# Revit family: Water_Heater-Commercial-Condensing-Lochinvar-Shield-SWH_Series
name_source: partatom
category: Mechanical Equipment
revit_build: Autodesk Revit 2016 (Build: 20150714_1515(x64)
units: mm (PartAtom-declared; Revit-internal decimal feet)

## family parameters
Cut with Voids When Loaded = No
Host = Face
OmniClass Number = 23.65.35.11
OmniClass Title = Supply Water Heaters
Part Type = Normal
Room Calculation Point = No
Round Connector Dimension = Use Diameter
Shared = Yes

## types (10) — shared parameters
Amperage 1 Phase - 120V - 60Hz = Yes
Assembly Code = D3020100
Audible Alarm Kit = No
BACnet Communication = No
CON·X·US® Remote Connectivity = No
Cold Water Connection Description = Cold Water Connection Inlet 1 1/2"
Cold Water Connection Diameter = 1 1/2"
Concentric Vent Kit = No
Condensate Drain Connection Diameter = 3/4"
Condensate Neutralization Kit = No
Default Elevation = 0"
Description = SHIELD COMMERCIAL WATER HEATER
Direct Venting = Yes
Drain Connection Diameter = 3/4"
Drain Radius = 3/8"
Finish = Metal-Lochinvar-Steel/Glass-Lined
Fuel Type = N - Natural Gas
Hot Water Connection Description = Hot Water Connection Outlet 1 1/2"
Hot Water Connection Diameter = 2"
Inlet D from Front Central = 3"
L - LP Gas = No
Low Water Cutoff Kit = No
Manufacturer = Lochinvar
Material = Metal-Lochinvar-Steel/Glass-Lined
Modbus Communication = No
N - Natural Gas = Yes
Operating Temperature = up to 180˚F
Outlet D From Right Edge = 2 21/32"
Power Supply Description = 120V/1PH/60Hz Power Supply
Price = Prices may vary. Please consult Manufacturer Representative for most up-to-date price list.
Product Documentation Link = https://www.lochinvar.com
Product Page URL = https://www.lochinvar.com
Sidewall Vent Termination Kit = No
T & P Connection Description = 3/4" Relief Connection
T & P Valve Opening Diameter = 3/4"
Turn-Down = 5:1
URL = http://www.lochinvar.com
Vent Cover Plate = No
Voltage = 120 V
Warranty Documentation Link = https://www.lochinvar.com
Water conn Radius = 3/4"
Working Pressure = 150.00 psi

## per-type parameters (varying)
- SWR125*: A=62 1/2"; ASME Tank Construction=No; Air Inlet D From Front Center=1 1/2"; Air Inlet D from Right Edge=6 27/32"; Air Inlet Radius=1 1/2"; Air Intake Connection Description=Air Intake Connection 3''; Air Intake Connection Diameter=3"; B=28"; BTU/hr Input=125000.0 Btu/h; Control Panel Radius1=14 1/2"; Control Panel Radius2=15"; D=29 1/2"; E=46 1/2"; Exhaust Air Connection Description=Exhaust Air Connection 3"; Exhaust Air Connection Diameter=3"; Flue D-from-Center=4"; Flue vent Dia.=3"; Flue vent radius=1 1/2"; GPH @ 100° Rise=145; Gallons Storage=65; Gas Connection Description=Gas Supply Connection 1/2"; Gas Off from side Center=5"; Gas Supply Connection Diameter=1/2"; Gas conn Radius=1/4"; Gas off From Front Center=11 1/4"; Height=66"; Inlet D From Right edge=4 1/2"; LP Connection Description=LP Supply Connection 1/2"; Outlet D From Front Central=2 7/8"; Power D From Center=4 15/32"; Power D From Front=1 3/4"; Shipping Weight=377 LBS.; T&P Off from Center=1 7/8"; Tank Radius=14"; Thermal Efficiency=96%
- SWR150*: A=76"; ASME Tank Construction=No; Air Inlet D From Front Center=1 1/2"; Air Inlet D from Right Edge=4 3/32"; Air Inlet Radius=1 1/2"; Air Intake Connection Description=Air Intake Connection 3''; Air Intake Connection Diameter=3"; B=28"; BTU/hr Input=150000.0 Btu/h; Control Panel Radius1=14 1/2"; Control Panel Radius2=15"; D=44"; E=61"; Exhaust Air Connection Description=Exhaust Air Connection 3"; Exhaust Air Connection Diameter=3"; Flue D-from-Center=4"; Flue vent Dia.=3"; Flue vent radius=1 1/2"; GPH @ 100° Rise=175; Gallons Storage=90; Gas Connection Description=Gas Supply Connection 1/2"; Gas Off from side Center=5"; Gas Supply Connection Diameter=1/2"; Gas conn Radius=1/4"; Gas off From Front Center=11 1/4"; Height=79 1/2"; Inlet D From Right edge=4 1/2"; LP Connection Description=LP Supply Connection 1/2"; Outlet D From Front Central=4 7/8"; Power D From Center=4 15/32"; Power D From Front=1 3/4"; Shipping Weight=700 LBS.; T&P Off from Center=1 7/8"; Tank Radius=14"; Thermal Efficiency=96%
- SWR200*: A=76"; ASME Tank Construction=No; Air Inlet D From Front Center=6"; Air Inlet D from Right Edge=3 19/32"; Air Inlet Radius=1 1/2"; Air Intake Connection Description=Air Intake Connection 3''; Air Intake Connection Diameter=3"; B=28"; BTU/hr Input=199000.0 Btu/h; Control Panel Radius1=14 1/2"; Control Panel Radius2=15"; D=44"; E=61"; Exhaust Air Connection Description=Exhaust Air Connection 3"; Exhaust Air Connection Diameter=3"; Flue D-from-Center=4"; Flue vent Dia.=3"; Flue vent radius=1 1/2"; GPH @ 100° Rise=233; Gallons Storage=90; Gas Connection Description=Gas Supply Connection 1/2"; Gas Off from side Center=5"; Gas Supply Connection Diameter=1/2"; Gas conn Radius=1/4"; Gas off From Front Center=11 1/4"; Height=79 1/2"; Inlet D From Right edge=4 1/2"; LP Connection Description=LP Supply Connection 1/2"; Outlet D From Front Central=3 3/8"; Power D From Center=4 15/32"; Power D From Front=1 3/4"; Shipping Weight=725 LBS.; T&P Off from Center=1 7/8"; Tank Radius=14"; Thermal Efficiency=96%
- SWR285*: A=77 1/2"; ASME Tank Construction=No; Air Inlet D From Front Center=8 3/4"; Air Inlet D from Right Edge=5 19/32"; Air Inlet Radius=2"; Air Intake Connection Description=Air Intake Connection 4''; Air Intake Connection Diameter=4"; B=34"; BTU/hr Input=285000.0 Btu/h; Control Panel Radius1=17 1/2"; Control Panel Radius2=18"; D=30 1/2"; E=51 3/4"; Exhaust Air Connection Description=Exhaust Air Connection 4"; Exhaust Air Connection Diameter=4"; Flue D-from-Center=1/4"; Flue vent Dia.=4"; Flue vent radius=2"; GPH @ 100° Rise=328; Gallons Storage=110; Gas Connection Description=Gas Supply Connection 3/4"; Gas Off from side Center=12 1/2"; Gas Supply Connection Diameter=3/4"; Gas conn Radius=3/8"; Gas off From Front Center=8"; Height=79 3/8"; Inlet D From Right edge=2 1/2"; LP Connection Description=LP Supply Connection 3/4"; Outlet D From Front Central=3 3/8"; Power D From Center=2 7/32"; Power D From Front=1 1/4"; Shipping Weight=800 LBS.; T&P Off from Center=1 7/8"; Tank Radius=17"; Thermal Efficiency=95%
- SWR400*: A=77 1/2"; ASME Tank Construction=No; Air Inlet D From Front Center=5 3/4"; Air Inlet D from Right Edge=5 3/32"; Air Inlet Radius=2"; Air Intake Connection Description=Air Intake Connection 4''; Air Intake Connection Diameter=4"; B=34"; BTU/hr Input=399000.0 Btu/h; Control Panel Radius1=17 1/2"; Control Panel Radius2=18"; D=30 1/2"; E=51 3/4"; Exhaust Air Connection Description=Exhaust Air Connection 4"; Exhaust Air Connection Diameter=4"; Flue D-from-Center=14"; Flue vent Dia.=4"; Flue vent radius=2"; GPH @ 100° Rise=459; Gallons Storage=110; Gas Connection Description=Gas Supply Connection 1"; Gas Off from side Center=9 1/2"; Gas Supply Connection Diameter=1"; Gas conn Radius=1/2"; Gas off From Front Center=11 3/4"; Height=79 3/8"; Inlet D From Right edge=2 1/2"; LP Connection Description=LP Supply Connection 1"; Outlet D From Front Central=3 3/8"; Power D From Center=2 7/32"; Power D From Front=1 1/4"; Shipping Weight=850 LBS.; T&P Off from Center=1 7/8"; Tank Radius=17"; Thermal Efficiency=95%
- SWA150*: A=76"; ASME Tank Construction=Yes; Air Inlet D From Front Center=1 1/2"; Air Inlet D from Right Edge=4 3/32"; Air Inlet Radius=1 1/2"; Air Intake Connection Description=Air Intake Connection 3''; Air Intake Connection Diameter=3"; B=28"; BTU/hr Input=150000.0 Btu/h; Control Panel Radius1=14 1/2"; Control Panel Radius2=15"; D=44"; E=61"; Exhaust Air Connection Description=Exhaust Air Connection 3"; Exhaust Air Connection Diameter=3"; Flue D-from-Center=4"; Flue vent Dia.=3"; Flue vent radius=1 1/2"; GPH @ 100° Rise=175; Gallons Storage=90; Gas Connection Description=Gas Supply Connection 1/2"; Gas Off from side Center=5"; Gas Supply Connection Diameter=1/2"; Gas conn Radius=1/4"; Gas off From Front Center=11 1/4"; Height=79 1/2"; Inlet D From Right edge=4 1/2"; LP Connection Description=LP Supply Connection 1/2"; Outlet D From Front Central=4 7/8"; Power D From Center=4 15/32"; Power D From Front=1 3/4"; Shipping Weight=700 LBS.; T&P Off from Center=1 7/8"; Tank Radius=14"; Thermal Efficiency=96%
- SWA200*: A=76"; ASME Tank Construction=Yes; Air Inlet D From Front Center=6"; Air Inlet D from Right Edge=3 19/32"; Air Inlet Radius=1 1/2"; Air Intake Connection Description=Air Intake Connection 3''; Air Intake Connection Diameter=3"; B=28"; BTU/hr Input=199000.0 Btu/h; Control Panel Radius1=14 1/2"; Control Panel Radius2=15"; D=44"; E=61"; Exhaust Air Connection Description=Exhaust Air Connection 3"; Exhaust Air Connection Diameter=3"; Flue D-from-Center=4"; Flue vent Dia.=3"; Flue vent radius=1 1/2"; GPH @ 100° Rise=232; Gallons Storage=90; Gas Connection Description=Gas Supply Connection 1/2"; Gas Off from side Center=5"; Gas Supply Connection Diameter=1/2"; Gas conn Radius=1/4"; Gas off From Front Center=11 1/4"; Height=79 1/2"; Inlet D From Right edge=4 1/2"; LP Connection Description=LP Supply Connection 1/2"; Outlet D From Front Central=3 3/8"; Power D From Center=4 15/32"; Power D From Front=1 3/4"; Shipping Weight=725 LBS.; T&P Off from Center=1 7/8"; Tank Radius=14"; Thermal Efficiency=96%
- SWA285*: A=77 1/2"; ASME Tank Construction=Yes; Air Inlet D From Front Center=8 3/4"; Air Inlet D from Right Edge=5 19/32"; Air Inlet Radius=2"; Air Intake Connection Description=Air Intake Connection 4''; Air Intake Connection Diameter=4"; B=34"; BTU/hr Input=285000.0 Btu/h; Control Panel Radius1=17 1/2"; Control Panel Radius2=18"; D=30 1/2"; E=51 3/4"; Exhaust Air Connection Description=Exhaust Air Connection 4"; Exhaust Air Connection Diameter=4"; Flue D-from-Center=1/4"; Flue vent Dia.=4"; Flue vent radius=2"; GPH @ 100° Rise=328; Gallons Storage=110; Gas Connection Description=Gas Supply Connection 3/4"; Gas Off from side Center=12 1/2"; Gas Supply Connection Diameter=3/4"; Gas conn Radius=3/8"; Gas off From Front Center=8"; Height=79 3/8"; Inlet D From Right edge=2 1/2"; LP Connection Description=LP Supply Connection 3/4"; Outlet D From Front Central=3 3/8"; Power D From Center=2 7/32"; Power D From Front=1 1/4"; Shipping Weight=800 LBS.; T&P Off from Center=1 7/8"; Tank Radius=17"; Thermal Efficiency=95%
- SWA400*: A=77 1/2"; ASME Tank Construction=Yes; Air Inlet D From Front Center=5 3/4"; Air Inlet D from Right Edge=5 3/32"; Air Inlet Radius=2"; Air Intake Connection Description=Air Intake Connection 4''; Air Intake Connection Diameter=4"; B=34"; BTU/hr Input=399000.0 Btu/h; Control Panel Radius1=17 1/2"; Control Panel Radius2=18"; D=30 1/2"; E=51 3/4"; Exhaust Air Connection Description=Exhaust Air Connection 4"; Exhaust Air Connection Diameter=4"; Flue D-from-Center=14"; Flue vent Dia.=4"; Flue vent radius=2"; GPH @ 100° Rise=459; Gallons Storage=110; Gas Connection Description=Gas Supply Connection 1"; Gas Off from side Center=9 1/2"; Gas Supply Connection Diameter=1"; Gas conn Radius=1/2"; Gas off From Front Center=11 3/4"; Height=79 3/8"; Inlet D From Right edge=2 1/2"; LP Connection Description=LP Supply Connection 1"; Outlet D From Front Central=3 3/8"; Power D From Center=2 7/32"; Power D From Front=1 1/4"; Shipping Weight=850 LBS.; T&P Off from Center=1 7/8"; Tank Radius=17"; Thermal Efficiency=95%
- SWA500*: A=77 1/2"; ASME Tank Construction=Yes; Air Inlet D From Front Center=5 3/4"; Air Inlet D from Right Edge=5 3/32"; Air Inlet Radius=2"; Air Intake Connection Description=Air Intake Connection 4''; Air Intake Connection Diameter=4"; B=34"; BTU/hr Input=500000.0 Btu/h; Control Panel Radius1=17 1/2"; Control Panel Radius2=18"; D=30 1/2"; E=51 3/4"; Exhaust Air Connection Description=Exhaust Air Connection 4"; Exhaust Air Connection Diameter=4"; Flue D-from-Center=14"; Flue vent Dia.=4"; Flue vent radius=2"; GPH @ 100° Rise=582; Gallons Storage=110; Gas Connection Description=Gas Supply Connection 1"; Gas Off from side Center=9 1/2"; Gas Supply Connection Diameter=1"; Gas conn Radius=1/2"; Gas off From Front Center=11 3/4"; Height=79 3/8"; Inlet D From Right edge=2 1/2"; LP Connection Description=LP Supply Connection 1"; Outlet D From Front Central=3 3/8"; Power D From Center=2 7/32"; Power D From Front=1 1/4"; Shipping Weight=875 LBS.; T&P Off from Center=6 7/8"; Tank Radius=17"; Thermal Efficiency=96%

note: column(s) folded — value = type name in every type: Model

## geometry (parser evidence)
native form markers: Sweep x5
no freeform markers — native parametric forms only
